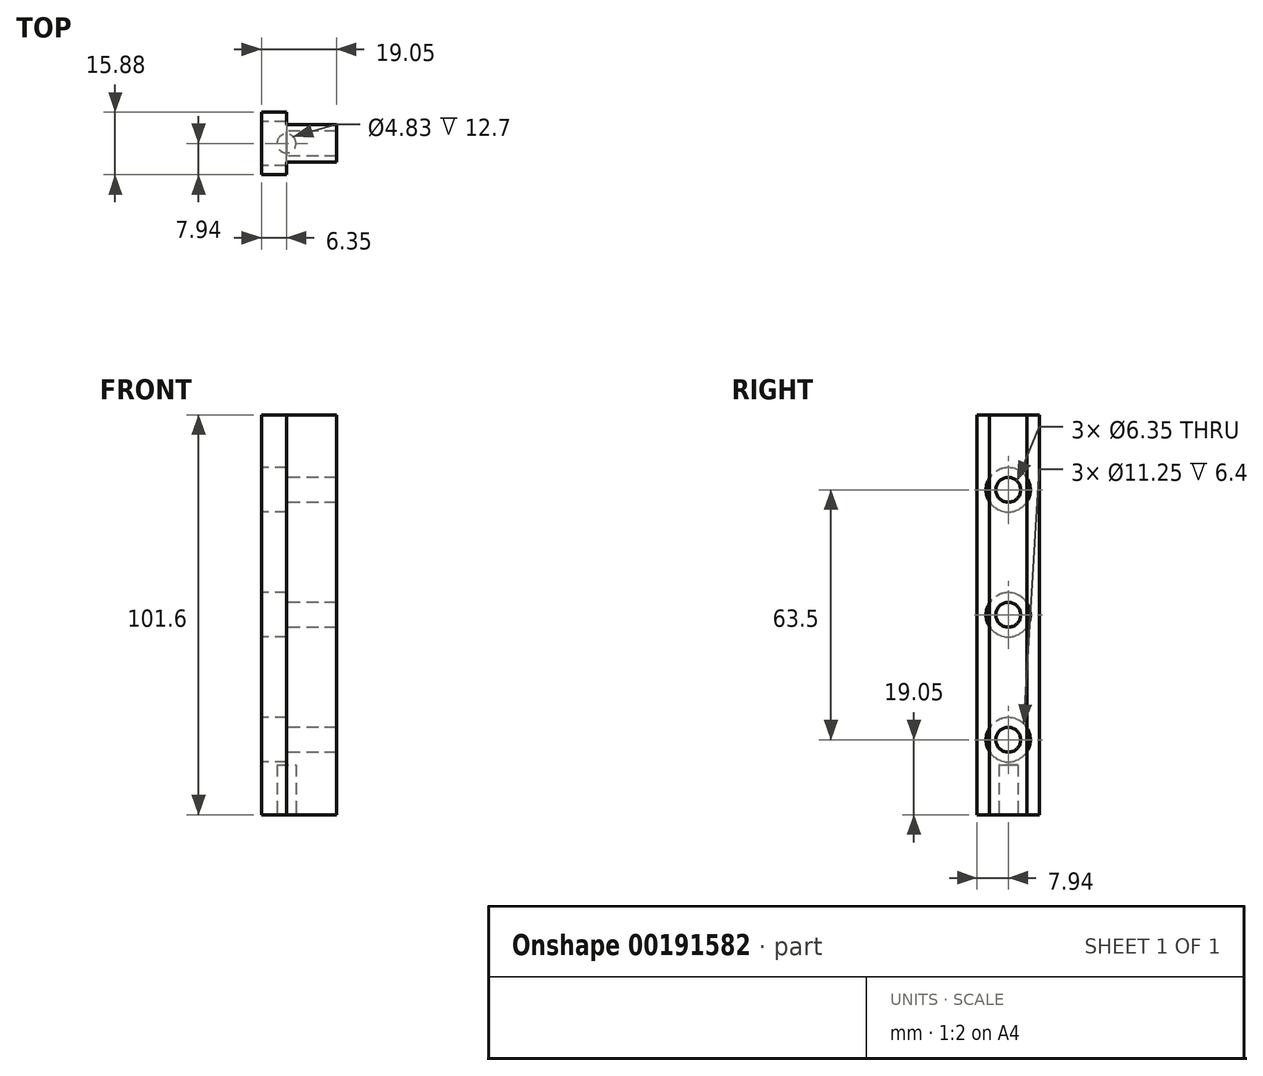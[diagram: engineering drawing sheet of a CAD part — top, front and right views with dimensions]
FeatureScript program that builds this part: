
annotation { "Feature Type Name" : "Feature", "Feature Type Description" : "" }
export const myFeature = defineFeature(function(context is Context, id is Id, definition is map)
    precondition{}
    {
        {
            var Q0;
            Q0=qCreatedBy(makeId("Top.planeOp"),FACE);
            var sketch = newSketch(context, id + "F0", { "sketchPlane" : qUnion([Q0])});
            skLineSegment(sketch, "E0", {"start": v(0, 7.94) * mm, "end": v(6.35, 7.94) * mm});
            skLineSegment(sketch, "E1", {"start": v(6.35, 7.94) * mm, "end": v(6.35, 4.76) * mm});
            skLineSegment(sketch, "E2", {"start": v(6.35, 4.76) * mm, "end": v(16.64, 4.76) * mm});
            skLineSegment(sketch, "E3", {"start": v(16.64, 4.76) * mm, "end": v(16.64, 4.76) * mm});
            skLineSegment(sketch, "E4", {"start": v(16.64, 4.76) * mm, "end": v(19.05, 4.76) * mm});
            skLineSegment(sketch, "E5", {"start": v(19.05, 4.76) * mm, "end": v(19.05, -4.76) * mm});
            skLineSegment(sketch, "E6", {"start": v(19.05, -4.76) * mm, "end": v(16.64, -4.76) * mm});
            skLineSegment(sketch, "E7", {"start": v(16.64, -4.76) * mm, "end": v(16.64, -4.76) * mm});
            skLineSegment(sketch, "E8", {"start": v(16.64, -4.76) * mm, "end": v(6.35, -4.76) * mm});
            skLineSegment(sketch, "E9", {"start": v(6.35, -4.76) * mm, "end": v(6.35, -7.94) * mm});
            skLineSegment(sketch, "E10", {"start": v(6.35, -7.94) * mm, "end": v(0, -7.94) * mm});
            skLineSegment(sketch, "E11", {"start": v(0, 7.94) * mm, "end": v(0, -7.94) * mm});
            skLineSegment(sketch, "E12", {"start": v(19.05, 0) * mm, "end": v(0, 0) * mm, "construction": true});
            skSolve(sketch);
        }
        {
            var Q0;
            Q0=makeQuery(id+"F0.imprint","IMPRINT",FACE,{"disambiguationData":[TD([[makeQuery(id+"F0.imprint","IMPRINT",EDGE,{"derivedFrom":sQuery(id+"F0.wireOp",EDGE,"E0")}),-1.0]])]});
            extrude(context, id + "F1", {"entities" : qUnion([Q0]), "endBound" : BoundingType.SYMMETRIC, "offsetDistance" : 25.4 * mm, "depth" : 101.6 * mm});
        }
        {
            var Q0;
            Q0=makeQuery(id+"F1.opExtrude","SWEPT_FACE",FACE,{"disambiguationData":[OSD([sQuery(id+"F0.wireOp",EDGE,"E11")])]});
            var sketch = newSketch(context, id + "F2", { "sketchPlane" : qUnion([Q0])});
            skCircle(sketch, "E13", {"center": v(0, -31.75) * mm, "radius": 3.18 * mm});
            skCircle(sketch, "E14", {"center": v(0, 0) * mm, "radius": 3.18 * mm});
            skCircle(sketch, "E15", {"center": v(0, 31.75) * mm, "radius": 3.18 * mm});
            skSolve(sketch);
        }
        {
            var Q0;
            Q0=makeQuery(id+"F2.imprint","IMPRINT",FACE,{"disambiguationData":[TD([[makeQuery(id+"F2.imprint","IMPRINT",EDGE,{"derivedFrom":sQuery(id+"F2.wireOp",EDGE,"E15")}),1.0]])]});
            var Q1;
            Q1=makeQuery(id+"F2.imprint","IMPRINT",FACE,{"disambiguationData":[TD([[makeQuery(id+"F2.imprint","IMPRINT",EDGE,{"derivedFrom":sQuery(id+"F2.wireOp",EDGE,"E14")}),1.0]])]});
            var Q2;
            Q2=makeQuery(id+"F2.imprint","IMPRINT",FACE,{"disambiguationData":[TD([[makeQuery(id+"F2.imprint","IMPRINT",EDGE,{"derivedFrom":sQuery(id+"F2.wireOp",EDGE,"E13")}),1.0]])]});
            extrude(context, id + "F3", {"entities" : qUnion([Q0, Q1, Q2]), "operationType" : NewBodyOperationType.REMOVE, "endBound" : BoundingType.THROUGH_ALL, "oppositeDirection" : true, "depth" : 25.4 * mm});
        }
        {
            var Q0;
            Q0=makeQuery(id+"F1.opExtrude","SWEPT_FACE",FACE,{"disambiguationData":[OSD([sQuery(id+"F0.wireOp",EDGE,"E11")])]});
            var sketch = newSketch(context, id + "F4", { "sketchPlane" : qUnion([Q0])});
            skCircle(sketch, "E16", {"center": v(0, 31.75) * mm, "radius": 5.62 * mm});
            skCircle(sketch, "E17", {"center": v(0, 0) * mm, "radius": 5.62 * mm});
            skCircle(sketch, "E18", {"center": v(0, -31.75) * mm, "radius": 5.62 * mm});
            skSolve(sketch);
        }
        {
            var Q0;
            Q0=makeQuery(id+"F4.imprint","IMPRINT",FACE,{"disambiguationData":[TD([[makeQuery(id+"F4.imprint","IMPRINT",EDGE,{"derivedFrom":sQuery(id+"F4.wireOp",EDGE,"E16")}),1.0]])]});
            var Q1;
            Q1=makeQuery(id+"F4.imprint","IMPRINT",FACE,{"disambiguationData":[TD([[makeQuery(id+"F4.imprint","IMPRINT",EDGE,{"derivedFrom":sQuery(id+"F4.wireOp",EDGE,"E17")}),1.0]])]});
            var Q2;
            Q2=makeQuery(id+"F4.imprint","IMPRINT",FACE,{"disambiguationData":[TD([[makeQuery(id+"F4.imprint","IMPRINT",EDGE,{"derivedFrom":sQuery(id+"F4.wireOp",EDGE,"E18")}),1.0]])]});
            extrude(context, id + "F5", {"entities" : qUnion([Q0, Q1, Q2]), "operationType" : NewBodyOperationType.REMOVE, "oppositeDirection" : true, "depth" : 6.4 * mm});
        }
        {
            var Q0;
            Q0=makeQuery(id+"F1.opExtrude","CAP_FACE",FACE,{"disambiguationData":[OSD([sQuery(id+"F0.wireOp",EDGE,"E0"),sQuery(id+"F0.wireOp",EDGE,"E1"),sQuery(id+"F0.wireOp",EDGE,"E2"),sQuery(id+"F0.wireOp",EDGE,"E4"),sQuery(id+"F0.wireOp",EDGE,"E5"),sQuery(id+"F0.wireOp",EDGE,"E6"),sQuery(id+"F0.wireOp",EDGE,"E8"),sQuery(id+"F0.wireOp",EDGE,"E9"),sQuery(id+"F0.wireOp",EDGE,"E10"),sQuery(id+"F0.wireOp",EDGE,"E11")])],"isStart":true});
            var sketch = newSketch(context, id + "F6", { "sketchPlane" : qUnion([Q0])});
            skCircle(sketch, "E19", {"center": v(6.35, 0) * mm, "radius": 2.41 * mm});
            skSolve(sketch);
        }
        {
            var Q0;
            Q0=makeQuery(id+"F6.imprint","IMPRINT",FACE,{"disambiguationData":[TD([[makeQuery(id+"F6.imprint","IMPRINT",EDGE,{"derivedFrom":sQuery(id+"F6.wireOp",EDGE,"E19")}),1.0]])]});
            extrude(context, id + "F7", {"entities" : qUnion([Q0]), "operationType" : NewBodyOperationType.REMOVE, "oppositeDirection" : true, "depth" : 12.7 * mm});
        }
    });
